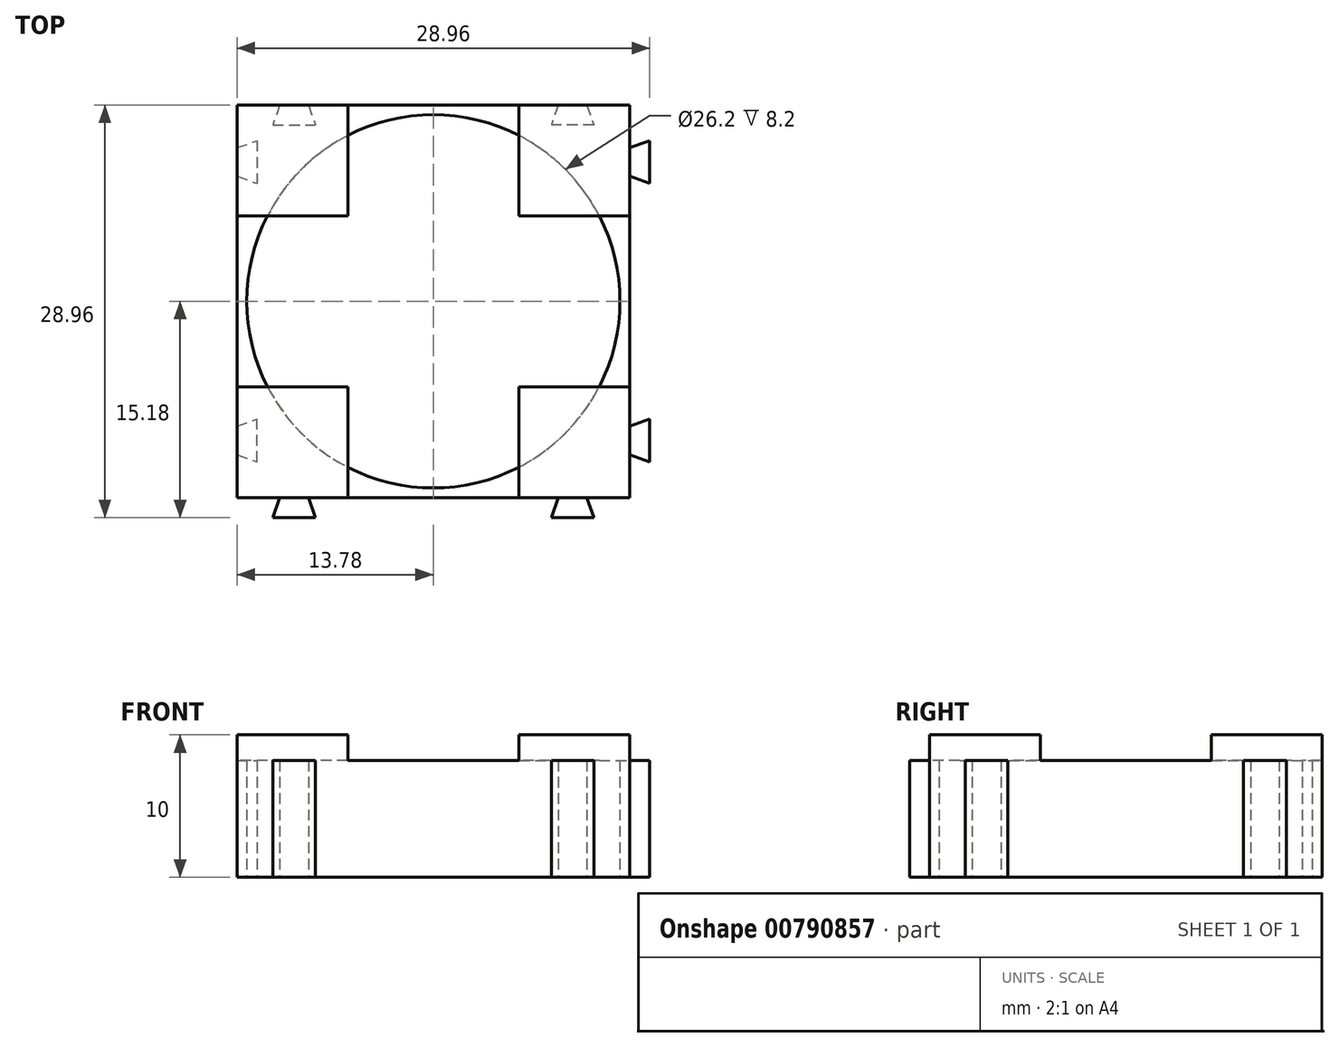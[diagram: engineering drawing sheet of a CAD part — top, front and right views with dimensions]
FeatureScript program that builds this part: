
annotation { "Feature Type Name" : "Feature", "Feature Type Description" : "" }
export const myFeature = defineFeature(function(context is Context, id is Id, definition is map)
    precondition{}
    {
        {
            var Q0;
            Q0=qCreatedBy(makeId("Top.planeOp"),FACE);
            var sketch = newSketch(context, id + "F0", { "sketchPlane" : qUnion([Q0])});
            skLineSegment(sketch, "E0.bottom", {"start": v(13.78, 13.78) * mm, "end": v(-13.78, 13.78) * mm});
            skLineSegment(sketch, "E0.top", {"start": v(13.78, -13.78) * mm, "end": v(-13.78, -13.78) * mm});
            skLineSegment(sketch, "E0.left", {"start": v(13.78, 13.78) * mm, "end": v(13.78, -13.78) * mm});
            skLineSegment(sketch, "E0.right", {"start": v(-13.78, 13.78) * mm, "end": v(-13.78, -13.78) * mm});
            skPoint(sketch, "E0.middle", {"position": v(0, 0) * mm});
            skCircle(sketch, "E1", {"center": v(0, 0) * mm, "radius": 13.1 * mm});
            skLineSegment(sketch, "E2", {"start": v(-11.28, 12.38) * mm, "end": v(-8.27, 12.38) * mm});
            skLineSegment(sketch, "E3", {"start": v(0, -13.78) * mm, "end": v(0, 13.78) * mm});
            skLineSegment(sketch, "E4", {"start": v(13.78, 0) * mm, "end": v(-13.78, 0) * mm});
            skLineSegment(sketch, "E5", {"start": v(-13.77, 13.78) * mm, "end": v(13.77, -13.78) * mm});
            skLineSegment(sketch, "E6", {"start": v(-9.77, 12.38) * mm, "end": v(-9.77, 13.78) * mm});
            skLineSegment(sketch, "E7", {"start": v(-9.77, 13.78) * mm, "end": v(-8.77, 13.78) * mm});
            skLineSegment(sketch, "E8", {"start": v(-8.78, 13.77) * mm, "end": v(-8.28, 12.37) * mm});
            skLineSegment(sketch, "E9.MirrorCS", {"start": v(-10.77, 13.77) * mm, "end": v(-11.27, 12.37) * mm});
            skLineSegment(sketch, "E10.MirrorCS", {"start": v(10.77, 13.77) * mm, "end": v(11.28, 12.37) * mm});
            skLineSegment(sketch, "E11.MirrorCS", {"start": v(11.28, 12.38) * mm, "end": v(8.27, 12.38) * mm});
            skLineSegment(sketch, "E12.MirrorCS", {"start": v(8.78, 13.77) * mm, "end": v(8.28, 12.37) * mm});
            skLineSegment(sketch, "E13.MirrorCS", {"start": v(-13.77, 10.77) * mm, "end": v(-12.38, 11.27) * mm});
            skLineSegment(sketch, "E14.MirrorCS", {"start": v(-12.38, 11.27) * mm, "end": v(-12.38, 8.27) * mm});
            skLineSegment(sketch, "E15.MirrorCS", {"start": v(-13.78, 8.78) * mm, "end": v(-12.38, 8.27) * mm});
            skLineSegment(sketch, "E16.MirrorCS", {"start": v(-13.77, -8.78) * mm, "end": v(-12.37, -8.28) * mm});
            skLineSegment(sketch, "E17.MirrorCS", {"start": v(-12.38, -11.28) * mm, "end": v(-12.38, -8.27) * mm});
            skLineSegment(sketch, "E18.MirrorCS", {"start": v(-13.77, -10.78) * mm, "end": v(-12.38, -11.28) * mm});
            skLineSegment(sketch, "E19", {"start": v(-11.28, -15.18) * mm, "end": v(-8.28, -15.18) * mm});
            skLineSegment(sketch, "E20", {"start": v(-10.78, -13.78) * mm, "end": v(-8.77, -13.78) * mm});
            skLineSegment(sketch, "E21", {"start": v(-10.77, -13.78) * mm, "end": v(-11.28, -15.18) * mm});
            skLineSegment(sketch, "E22", {"start": v(-8.78, -13.78) * mm, "end": v(-8.27, -15.17) * mm});
            skLineSegment(sketch, "E23.MirrorCS", {"start": v(8.78, -13.78) * mm, "end": v(8.27, -15.17) * mm});
            skLineSegment(sketch, "E24.MirrorCS", {"start": v(11.28, -15.18) * mm, "end": v(8.28, -15.18) * mm});
            skLineSegment(sketch, "E25.MirrorCS", {"start": v(10.77, -13.78) * mm, "end": v(11.28, -15.18) * mm});
            skLineSegment(sketch, "E26.MirrorCS", {"start": v(13.78, -10.77) * mm, "end": v(15.18, -11.28) * mm});
            skLineSegment(sketch, "E27.MirrorCS", {"start": v(15.18, -11.28) * mm, "end": v(15.18, -8.28) * mm});
            skLineSegment(sketch, "E28.MirrorCS", {"start": v(13.78, -8.78) * mm, "end": v(15.17, -8.27) * mm});
            skLineSegment(sketch, "E29.MirrorCS", {"start": v(13.78, 8.78) * mm, "end": v(15.17, 8.27) * mm});
            skLineSegment(sketch, "E30.MirrorCS", {"start": v(15.17, 11.28) * mm, "end": v(15.17, 8.28) * mm});
            skLineSegment(sketch, "E31.MirrorCS", {"start": v(13.78, 10.77) * mm, "end": v(15.17, 11.28) * mm});
            skLineSegment(sketch, "E32.direction1", {"start": v(-13.78, -13.78) * mm, "end": v(13.77, -13.78) * mm, "construction": true});
            skSolve(sketch);
        }
        {
            var Q0;
            {var subQ4=sQuery(id+"F0.wireOp",EDGE,"E10.MirrorCS");Q0=makeQuery(id+"F0.imprint","IMPRINT",FACE,{"disambiguationData":[TD([[makeQuery(id+"F0.imprint","IMPRINT",EDGE,{"derivedFrom":subQ4}),1.0]])]});}
            var Q1;
            {var subQ0=sQuery(id+"F0.wireOp",EDGE,"E29.MirrorCS");Q1=makeQuery(id+"F0.imprint","IMPRINT",FACE,{"disambiguationData":[TD([[makeQuery(id+"F0.imprint","IMPRINT",EDGE,{"derivedFrom":subQ0}),1.0]])]});}
            var Q2;
            {var subQ0=sQuery(id+"F0.wireOp",EDGE,"E26.MirrorCS");Q2=makeQuery(id+"F0.imprint","IMPRINT",FACE,{"disambiguationData":[TD([[makeQuery(id+"F0.imprint","IMPRINT",EDGE,{"derivedFrom":subQ0}),1.0]])]});}
            var Q3;
            {var subQ0=sQuery(id+"F0.wireOp",EDGE,"E4");var subQ5=sQuery(id+"F0.wireOp",EDGE,"E0.left");var subQ9=makeQuery(id+"F0.imprint","INTERSECT",VERTEX,{"derivedFrom":[subQ5,subQ0]});Q3=makeQuery(id+"F0.imprint","IMPRINT",FACE,{"disambiguationData":[TD([[makeQuery(id+"F0.imprint","IMPRINT",EDGE,{"disambiguationData":[TD([[subQ9,-1.0]])],"derivedFrom":subQ5}),-1.0]])]});}
            var Q4;
            {var subQ1=sQuery(id+"F0.wireOp",EDGE,"E0.top");var subQ3=makeQuery(id+"F0.imprint","INTERSECT",VERTEX,{"derivedFrom":[subQ1,sQuery(id+"F0.wireOp",EDGE,"E23.MirrorCS")]});Q4=makeQuery(id+"F0.imprint","IMPRINT",FACE,{"disambiguationData":[TD([[makeQuery(id+"F0.imprint","IMPRINT",EDGE,{"disambiguationData":[TD([[subQ3,1.0]])],"derivedFrom":subQ1}),-1.0]])]});}
            var Q5;
            {var subQ0=sQuery(id+"F0.wireOp",EDGE,"E23.MirrorCS");Q5=makeQuery(id+"F0.imprint","IMPRINT",FACE,{"disambiguationData":[TD([[makeQuery(id+"F0.imprint","IMPRINT",EDGE,{"derivedFrom":subQ0}),1.0]])]});}
            var Q6;
            {var subQ11=sQuery(id+"F0.wireOp",EDGE,"E16.MirrorCS");Q6=makeQuery(id+"F0.imprint","IMPRINT",FACE,{"disambiguationData":[TD([[makeQuery(id+"F0.imprint","IMPRINT",EDGE,{"derivedFrom":subQ11}),1.0]])]});}
            var Q7;
            Q7=makeQuery(id+"F0.imprint","IMPRINT",FACE,{"disambiguationData":[TD([[makeQuery(id+"F0.imprint","IMPRINT",EDGE,{"derivedFrom":sQuery(id+"F0.wireOp",EDGE,"E19")}),1.0]])]});
            var Q8;
            {var subQ9=sQuery(id+"F0.wireOp",EDGE,"E13.MirrorCS");Q8=makeQuery(id+"F0.imprint","IMPRINT",FACE,{"disambiguationData":[TD([[makeQuery(id+"F0.imprint","IMPRINT",EDGE,{"derivedFrom":subQ9}),1.0]])]});}
            var Q9;
            {var subQ11=sQuery(id+"F0.wireOp",EDGE,"E8");Q9=makeQuery(id+"F0.imprint","IMPRINT",FACE,{"disambiguationData":[TD([[makeQuery(id+"F0.imprint","IMPRINT",EDGE,{"derivedFrom":subQ11}),1.0]])]});}
            var Q10;
            {var subQ1=sQuery(id+"F0.wireOp",EDGE,"E4");var subQ4=sQuery(id+"F0.wireOp",EDGE,"E1");var subQ5=makeQuery(id+"F0.imprint","INTERSECT",VERTEX,{"disambiguationData":[OD(0.0)],"derivedFrom":[subQ4,subQ1]});Q10=makeQuery(id+"F0.imprint","IMPRINT",FACE,{"disambiguationData":[TD([[makeQuery(id+"F0.imprint","IMPRINT",EDGE,{"disambiguationData":[TD([[subQ5,1.0]])],"derivedFrom":subQ4}),-1.0]])]});}
            var Q11;
            Q11=makeQuery(id+"F0.imprint","IMPRINT",FACE,{"disambiguationData":[TD([[makeQuery(id+"F0.imprint","IMPRINT",EDGE,{"derivedFrom":sQuery(id+"F0.wireOp",EDGE,"E32.1.0.12")}),-1.0]])]});
            var Q12;
            Q12=makeQuery(id+"F0.imprint","IMPRINT",FACE,{"disambiguationData":[TD([[makeQuery(id+"F0.imprint","IMPRINT",EDGE,{"derivedFrom":sQuery(id+"F0.wireOp",EDGE,"E32.1.0.12")}),1.0]])]});
            var Q13;
            Q13=makeQuery(id+"F0.imprint","IMPRINT",FACE,{"disambiguationData":[TD([[makeQuery(id+"F0.imprint","IMPRINT",EDGE,{"derivedFrom":sQuery(id+"F0.wireOp",EDGE,"E32.1.0.14")}),-1.0]])]});
            var Q14;
            Q14=makeQuery(id+"F0.imprint","IMPRINT",FACE,{"disambiguationData":[TD([[makeQuery(id+"F0.imprint","IMPRINT",EDGE,{"derivedFrom":sQuery(id+"F0.wireOp",EDGE,"E32.1.0.14")}),1.0]])]});
            var Q15;
            {var subQ13=sQuery(id+"F0.wireOp",EDGE,"E32.1.0.30");Q15=makeQuery(id+"F0.imprint","IMPRINT",FACE,{"disambiguationData":[TD([[makeQuery(id+"F0.imprint","IMPRINT",EDGE,{"derivedFrom":subQ13}),1.0]])]});}
            var Q16;
            {var subQ1=sQuery(id+"F0.wireOp",EDGE,"E0.bottom");var subQ3=sQuery(id+"F0.wireOp",EDGE,"E32.1.0.7");var subQ4=makeQuery(id+"F0.imprint","INTERSECT",VERTEX,{"derivedFrom":[subQ1,subQ3]});Q16=makeQuery(id+"F0.imprint","IMPRINT",FACE,{"disambiguationData":[TD([[makeQuery(id+"F0.imprint","IMPRINT",EDGE,{"disambiguationData":[TD([[subQ4,1.0]])],"derivedFrom":subQ3}),-1.0]])]});}
            var Q17;
            {var subQ1=sQuery(id+"F0.wireOp",EDGE,"E32.1.0.4");var subQ3=sQuery(id+"F0.wireOp",EDGE,"E32.1.0.7");var subQ4=makeQuery(id+"F0.imprint","INTERSECT",VERTEX,{"derivedFrom":[subQ1,subQ3]});Q17=makeQuery(id+"F0.imprint","IMPRINT",FACE,{"disambiguationData":[TD([[makeQuery(id+"F0.imprint","IMPRINT",EDGE,{"disambiguationData":[TD([[subQ4,1.0]])],"derivedFrom":subQ3}),-1.0]])]});}
            var Q18;
            {var subQ1=sQuery(id+"F0.wireOp",EDGE,"E32.1.0.1");var subQ3=sQuery(id+"F0.wireOp",EDGE,"E32.1.0.7");var subQ4=makeQuery(id+"F0.imprint","INTERSECT",VERTEX,{"derivedFrom":[subQ1,subQ3]});Q18=makeQuery(id+"F0.imprint","IMPRINT",FACE,{"disambiguationData":[TD([[makeQuery(id+"F0.imprint","IMPRINT",EDGE,{"disambiguationData":[TD([[subQ4,-1.0]])],"derivedFrom":subQ3}),-1.0]])]});}
            var Q19;
            Q19=makeQuery(id+"F0.imprint","IMPRINT",FACE,{"disambiguationData":[TD([[makeQuery(id+"F0.imprint","IMPRINT",EDGE,{"derivedFrom":sQuery(id+"F0.wireOp",EDGE,"E32.1.0.15")}),1.0]])]});
            var Q20;
            Q20=makeQuery(id+"F0.imprint","IMPRINT",FACE,{"disambiguationData":[TD([[makeQuery(id+"F0.imprint","IMPRINT",EDGE,{"derivedFrom":sQuery(id+"F0.wireOp",EDGE,"E32.1.0.32")}),-1.0]])]});
            var Q21;
            Q21=makeQuery(id+"F0.imprint","IMPRINT",FACE,{"disambiguationData":[TD([[makeQuery(id+"F0.imprint","IMPRINT",EDGE,{"derivedFrom":sQuery(id+"F0.wireOp",EDGE,"E32.1.0.8")}),1.0]])]});
            var Q22;
            Q22=makeQuery(id+"F0.imprint","IMPRINT",FACE,{"disambiguationData":[TD([[makeQuery(id+"F0.imprint","IMPRINT",EDGE,{"derivedFrom":sQuery(id+"F0.wireOp",EDGE,"E32.1.0.0")}),-1.0]])]});
            var Q23;
            {var subQ0=sQuery(id+"F0.wireOp",EDGE,"E32.1.0.35");Q23=makeQuery(id+"F0.imprint","IMPRINT",FACE,{"disambiguationData":[TD([[makeQuery(id+"F0.imprint","IMPRINT",EDGE,{"derivedFrom":subQ0}),-1.0]])]});}
            var Q24;
            {var subQ1=sQuery(id+"F0.wireOp",EDGE,"E32.1.0.3");var subQ5=sQuery(id+"F0.wireOp",EDGE,"E32.1.0.9");var subQ6=makeQuery(id+"F0.imprint","INTERSECT",VERTEX,{"derivedFrom":[subQ1,subQ5]});Q24=makeQuery(id+"F0.imprint","IMPRINT",FACE,{"disambiguationData":[TD([[makeQuery(id+"F0.imprint","IMPRINT",EDGE,{"disambiguationData":[TD([[subQ6,-1.0]])],"derivedFrom":subQ1}),-1.0]])]});}
            var Q25;
            {var subQ1=sQuery(id+"F0.wireOp",EDGE,"E32.1.0.2");var subQ4=makeQuery(id+"F0.imprint","INTERSECT",VERTEX,{"derivedFrom":[subQ1,sQuery(id+"F0.wireOp",EDGE,"E32.1.0.16")]});Q25=makeQuery(id+"F0.imprint","IMPRINT",FACE,{"disambiguationData":[TD([[makeQuery(id+"F0.imprint","IMPRINT",EDGE,{"disambiguationData":[TD([[subQ4,-1.0]])],"derivedFrom":subQ1}),-1.0]])]});}
            extrude(context, id + "F1", {"entities" : qUnion([Q0, Q1, Q2, Q3, Q4, Q5, Q6, Q7, Q8, Q9, Q10, Q11, Q12, Q13, Q14, Q15, Q16, Q17, Q18, Q19, Q20, Q21, Q22, Q23, Q24, Q25]), "depth" : (10 - 1.8) * mm, "offsetDistance" : 25 * mm});
        }
        {
            var Q0;
            Q0=makeQuery(id+"F1.opExtrude","CAP_FACE",FACE,{"disambiguationData":[OSD([sQuery(id+"F0.wireOp",EDGE,"E0.bottom"),sQuery(id+"F0.wireOp",EDGE,"E0.top"),sQuery(id+"F0.wireOp",EDGE,"E0.left"),sQuery(id+"F0.wireOp",EDGE,"E0.right"),sQuery(id+"F0.wireOp",EDGE,"E1"),sQuery(id+"F0.wireOp",EDGE,"E2"),sQuery(id+"F0.wireOp",EDGE,"E8"),sQuery(id+"F0.wireOp",EDGE,"E9.MirrorCS"),sQuery(id+"F0.wireOp",EDGE,"E10.MirrorCS"),sQuery(id+"F0.wireOp",EDGE,"E11.MirrorCS"),sQuery(id+"F0.wireOp",EDGE,"E12.MirrorCS"),sQuery(id+"F0.wireOp",EDGE,"E13.MirrorCS"),sQuery(id+"F0.wireOp",EDGE,"E14.MirrorCS"),sQuery(id+"F0.wireOp",EDGE,"E15.MirrorCS"),sQuery(id+"F0.wireOp",EDGE,"E16.MirrorCS"),sQuery(id+"F0.wireOp",EDGE,"E17.MirrorCS"),sQuery(id+"F0.wireOp",EDGE,"E18.MirrorCS"),sQuery(id+"F0.wireOp",EDGE,"E19"),sQuery(id+"F0.wireOp",EDGE,"E21"),sQuery(id+"F0.wireOp",EDGE,"E22"),sQuery(id+"F0.wireOp",EDGE,"E23.MirrorCS"),sQuery(id+"F0.wireOp",EDGE,"E24.MirrorCS"),sQuery(id+"F0.wireOp",EDGE,"E25.MirrorCS"),sQuery(id+"F0.wireOp",EDGE,"E26.MirrorCS"),sQuery(id+"F0.wireOp",EDGE,"E27.MirrorCS"),sQuery(id+"F0.wireOp",EDGE,"E28.MirrorCS"),sQuery(id+"F0.wireOp",EDGE,"E29.MirrorCS"),sQuery(id+"F0.wireOp",EDGE,"E30.MirrorCS"),sQuery(id+"F0.wireOp",EDGE,"E31.MirrorCS")])],"isStart":false});
            var sketch = newSketch(context, id + "F2", { "sketchPlane" : qUnion([Q0])});
            skLineSegment(sketch, "E33", {"start": v(-13.78, 13.78) * mm, "end": v(0, 0) * mm});
            skLineSegment(sketch, "E34", {"start": v(0, 0) * mm, "end": v(-13.78, -13.78) * mm});
            skLineSegment(sketch, "E35", {"start": v(-6, -6) * mm, "end": v(-13.78, -6) * mm});
            skLineSegment(sketch, "E36.MirrorCS", {"start": v(-6, -6) * mm, "end": v(-6, -13.77) * mm});
            skLineSegment(sketch, "E37", {"start": v(0, 0) * mm, "end": v(0, -20.67) * mm});
            skLineSegment(sketch, "E38.MirrorCS", {"start": v(6, -6) * mm, "end": v(6, -13.77) * mm});
            skLineSegment(sketch, "E39.MirrorCS", {"start": v(6, -6) * mm, "end": v(13.78, -6) * mm});
            skLineSegment(sketch, "E40", {"start": v(-13.78, -13.78) * mm, "end": v(-13.78, -6) * mm});
            skLineSegment(sketch, "E41", {"start": v(-13.78, -13.78) * mm, "end": v(-6, -13.78) * mm});
            skLineSegment(sketch, "E42.MirrorCS", {"start": v(13.78, -13.78) * mm, "end": v(6, -13.78) * mm});
            skLineSegment(sketch, "E43.MirrorCS", {"start": v(13.78, -13.78) * mm, "end": v(13.78, -6) * mm});
            skLineSegment(sketch, "E44.MirrorCS", {"start": v(-6, 6) * mm, "end": v(-13.77, 6) * mm});
            skLineSegment(sketch, "E45.MirrorCS", {"start": v(-6, 6) * mm, "end": v(-6, 13.77) * mm});
            skLineSegment(sketch, "E46.MirrorCS", {"start": v(-13.77, 13.78) * mm, "end": v(-6, 13.78) * mm});
            skLineSegment(sketch, "E47.MirrorCS", {"start": v(-13.77, 13.78) * mm, "end": v(-13.78, 6) * mm});
            skLineSegment(sketch, "E48.MirrorCS", {"start": v(6, 6) * mm, "end": v(6, 13.77) * mm});
            skLineSegment(sketch, "E49.MirrorCS", {"start": v(13.77, 13.78) * mm, "end": v(6, 13.78) * mm});
            skLineSegment(sketch, "E50.MirrorCS", {"start": v(13.77, 13.78) * mm, "end": v(13.78, 6) * mm});
            skLineSegment(sketch, "E51.MirrorCS", {"start": v(6, 6) * mm, "end": v(13.77, 6) * mm});
            skSolve(sketch);
        }
        {
            var Q0;
            Q0 = qSketchRegion(id + "F2", true);
            extrude(context, id + "F3", {"entities" : qUnion([Q0]), "operationType" : NewBodyOperationType.ADD, "depth" : 1.8 * mm, "offsetDistance" : 25 * mm});
        }
    });
